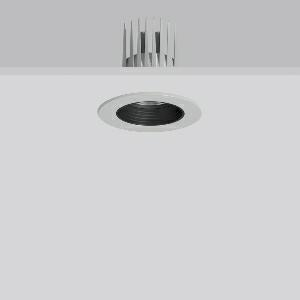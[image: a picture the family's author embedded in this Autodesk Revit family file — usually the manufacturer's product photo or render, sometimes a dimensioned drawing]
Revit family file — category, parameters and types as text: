
# Revit family: heledon_mini_e_901747_004_2_76_f9a2
name_source: partatom
category: Lighting Fixtures
units: mm (PartAtom-declared; Revit-internal decimal feet)

## family parameters
Cut with Voids When Loaded = No
Host = Face
Light Source = No
Part Type = Normal
Room Calculation Point = No
Round Connector Dimension = Use Diameter
Shared = No

## types (1)
- HELEDON mini E (1 x LED Modul 927, 1850 lm, 2700)
    Apparent Load = 20 VA
    Approval mark = CE
    CIE Flux Codes = 95 100 100 100 100
    Color Rendering = 92
    Color Temperature = 2700
    Default Elevation = 1800 mm
    Description = Series: HELEDON mini
Round recessed downlight. Housing: die-cast aluminium, powder-coated. Black plastic ring and recessed LED to prevent glare from the side. Optical assembly with lens made of plastic (polycarbonate) for the best homogeneous light distribution - can be changed without tools. Best colour rendering index Ra>90. Suitable for Recessed ceiling mounting. Installation without tools thanks to spring fastening system. Including separate LED converter with connecting cable 600 mm.High quality converter without flickering and stroboscopic effect. Through-wiring box (5 pole) available as accessory. The following accessories can be mounted without use of tools: interchangeable lenses, decorative glasses, honeycomb louvre, clear and frosted diffusers, white interchangeable plastic ring. 
Colour: silver
Diameter: 124 mm
Height: 3 mm
Cut-out diameter: 114 mm
Recess height: 170 mm
Luminaire: recess height: 120 mm
Lamp: LED
Socket: without socket
Colour temperature: 2700K
Colour rendering index (CRI): 92
System power: 20 W
Rated luminous flux: 1850 lm
Luminous efficiency: 93 lm/W
Control gear: Converter, dimmable, DALI
Protection class: II
Type of protection: IP 20
    Height = 0 mm  [stored 0 ft]
    Lamp = 1 x LED Modul 927
    Lamp Light Flux = 1850 lm
    Lamp count = 1
    Length = 124 mm  [stored 0.406824 ft]
    Lifetime = 50000 h
    Luminous efficacy = 93 lm/W
    Manufacturer = RZB
    ModVariant = No
    Model = 901747.004.2.76
    Mounting Place = Ceiling
    Mounting Type = Recessed
    Number of Poles = 1
    OnlyDefault = Yes
    Power Factor = 1
    Product Name = HELEDON mini E
    Product group = Recessed downlights
    ProductGroupID = 402
    Protection Class = Protection class II
    Protection Degree = IP 20
    RLX_Detail_Level = 1
    RLX_Emergency_Light_Flux = 0 lm
    RLX_Emergency_Type = 0
    RLX_Emergency_Type_DB = No
    RlxData = <blob elided: 136989 chars, md5=8214562c>
    Socket = socket
    Standby Power = 0 W
    System Light Flux = 1850 lm
    System Power = 20 W
    Type Comments = Product without accessories
    Type Image = 901656.004.jpg
    URL = http://relux.com
    VarID = ---
    Voltage = 230 V
    Voltage Range = 220-240 V
    Weight = 0.00 kg
    Width = 0 mm  [stored 0 ft]

note: [stored X ft] marks values corroborated as IEEE doubles in the binary element streams (Revit-internal decimal feet)

## geometry (parser evidence)
native form markers: Blend x4, Sweep x9
no freeform markers — native parametric forms only
